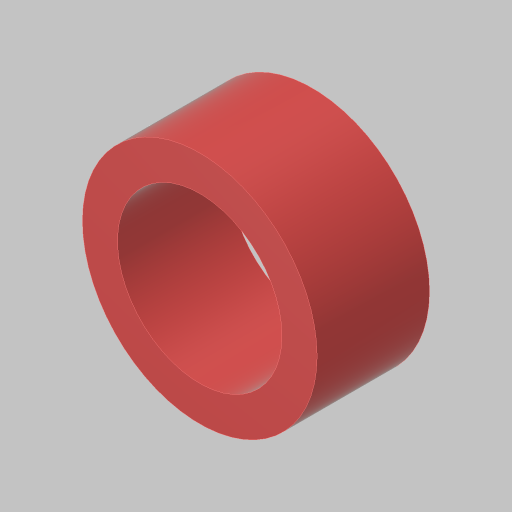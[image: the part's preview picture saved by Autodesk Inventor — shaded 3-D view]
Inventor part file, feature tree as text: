
AUTODESK INVENTOR PART (.ipt)
format: ipt  version: 2023.5 (Build 275446000, 446)  size: 116,224 bytes
history: native  units: in
note: dims shown in document units (in); Inventor stores cm internally (conversion verified against a paired STEP export)
features: extrude x1, sketch x1
ambient origin geometry x8: Origin, YZ Plane, XZ Plane, XY Plane, X Axis, Y Axis, Z Axis, Center Point
bodies: Solid1 (feature_tree)
feature tree (2):
  extrude  "Extrusion1"  Depth=0.4in
  sketch  "Sketch1"  dims[d0=0.585in d1=0.125in d2=0.4in d3=0.0in]
